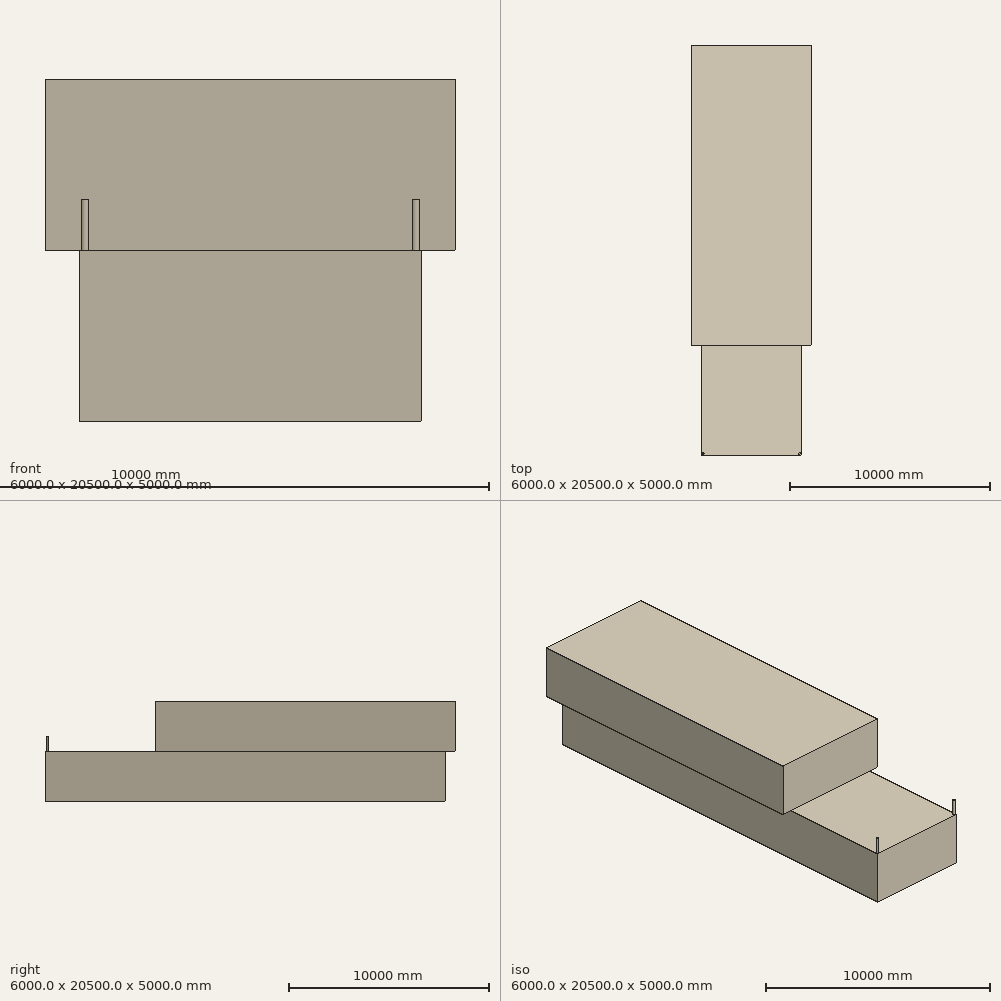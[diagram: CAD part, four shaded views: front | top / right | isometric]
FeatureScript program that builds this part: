
annotation { "Feature Type Name" : "Feature", "Feature Type Description" : "" }
export const myFeature = defineFeature(function(context is Context, id is Id, definition is map)
    precondition{}
    {
        {
            var Q0;
            Q0=qCreatedBy(makeId("Top.planeOp"),FACE);
            var sketch = newSketch(context, id + "F0", { "sketchPlane" : qUnion([Q0])});
            skLineSegment(sketch, "E0.bottom", {"start": v(0, 0) * mm, "end": v(-5000, 0) * mm});
            skLineSegment(sketch, "E0.top", {"start": v(0, 20000) * mm, "end": v(-5000, 20000) * mm});
            skLineSegment(sketch, "E0.left", {"start": v(0, 0) * mm, "end": v(0, 20000) * mm});
            skLineSegment(sketch, "E0.right", {"start": v(-5000, 0) * mm, "end": v(-5000, 20000) * mm});
            skSolve(sketch);
        }
        {
            var Q0;
            Q0=makeQuery(id+"F0.imprint","IMPRINT",FACE,{"disambiguationData":[TD([[makeQuery(id+"F0.imprint","IMPRINT",EDGE,{"derivedFrom":sQuery(id+"F0.wireOp",EDGE,"E0.bottom")}),-1.0]])]});
            extrude(context, id + "F1", {"entities" : qUnion([Q0]), "depth" : 2500 * mm});
        }
        {
            var Q0;
            Q0=makeQuery(id+"F1.opExtrude","CAP_FACE",FACE,{"disambiguationData":[OSD([sQuery(id+"F0.wireOp",EDGE,"E0.bottom"),sQuery(id+"F0.wireOp",EDGE,"E0.top"),sQuery(id+"F0.wireOp",EDGE,"E0.left"),sQuery(id+"F0.wireOp",EDGE,"E0.right")])],"isStart":false});
            var sketch = newSketch(context, id + "F2", { "sketchPlane" : qUnion([Q0])});
            skLineSegment(sketch, "E1.bottom", {"start": v(-5500, 5500) * mm, "end": v(500, 5500) * mm});
            skLineSegment(sketch, "E1.top", {"start": v(-5500, 20500) * mm, "end": v(500, 20500) * mm});
            skLineSegment(sketch, "E1.left", {"start": v(-5500, 5500) * mm, "end": v(-5500, 20500) * mm});
            skLineSegment(sketch, "E1.right", {"start": v(500, 5500) * mm, "end": v(500, 20500) * mm});
            skSolve(sketch);
        }
        {
            var Q0;
            Q0 = qSketchRegion(id + "F2", true);
            extrude(context, id + "F3", {"entities" : qUnion([Q0]), "operationType" : NewBodyOperationType.ADD, "depth" : 2500 * mm});
        }
        {
            var Q0;
            Q0=makeQuery(id+"F1.opExtrude","CAP_FACE",FACE,{"disambiguationData":[OSD([sQuery(id+"F0.wireOp",EDGE,"E0.bottom"),sQuery(id+"F0.wireOp",EDGE,"E0.top"),sQuery(id+"F0.wireOp",EDGE,"E0.left"),sQuery(id+"F0.wireOp",EDGE,"E0.right")])],"isStart":false});
            var sketch = newSketch(context, id + "F4", { "sketchPlane" : qUnion([Q0])});
            skCircle(sketch, "E2", {"center": v(-4920, 80) * mm, "radius": 50 * mm});
            skSolve(sketch);
        }
        {
            var Q0;
            Q0=makeQuery(id+"F4.imprint","IMPRINT",FACE,{"disambiguationData":[TD([[makeQuery(id+"F4.imprint","IMPRINT",EDGE,{"derivedFrom":sQuery(id+"F4.wireOp",EDGE,"E2")}),1.0]])]});
            extrude(context, id + "F5", {"entities" : qUnion([Q0]), "operationType" : NewBodyOperationType.ADD, "depth" : 750 * mm});
        }
        {
            var Q0;
            Q0=makeQuery(id+"F1.opExtrude","CAP_FACE",FACE,{"disambiguationData":[OSD([sQuery(id+"F0.wireOp",EDGE,"E0.bottom"),sQuery(id+"F0.wireOp",EDGE,"E0.top"),sQuery(id+"F0.wireOp",EDGE,"E0.left"),sQuery(id+"F0.wireOp",EDGE,"E0.right")])],"isStart":false});
            var sketch = newSketch(context, id + "F6", { "sketchPlane" : qUnion([Q0])});
            skCircle(sketch, "E3", {"center": v(-80, 80) * mm, "radius": 50 * mm});
            skSolve(sketch);
        }
        {
            var Q0;
            Q0=makeQuery(id+"F6.imprint","IMPRINT",FACE,{"disambiguationData":[TD([[makeQuery(id+"F6.imprint","IMPRINT",EDGE,{"derivedFrom":sQuery(id+"F6.wireOp",EDGE,"E3")}),1.0]])]});
            extrude(context, id + "F7", {"entities" : qUnion([Q0]), "operationType" : NewBodyOperationType.ADD, "depth" : 750 * mm});
        }
    });
